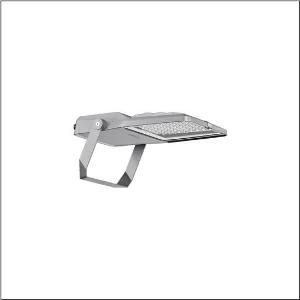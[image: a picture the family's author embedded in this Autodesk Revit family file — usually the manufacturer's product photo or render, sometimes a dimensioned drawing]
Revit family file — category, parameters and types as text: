
# Revit family: floodlight_fl_21_iq_mini___pl64_5xa7772b3e1a_f8e6
name_source: partatom
category: Lighting Fixtures
units: mm (PartAtom-declared; Revit-internal decimal feet)

## family parameters
Cut with Voids When Loaded = No
Host = Face
Light Source = No
Part Type = Normal
Room Calculation Point = No
Round Connector Dimension = Use Diameter
Shared = No

## types (1)
- --- (1 x LED, 5190 lm, 45.5 W, 3000K)
    Apparent Load = 46 VA
    CIE Flux Codes = 28 80 98 100 100
    Color Rendering = 80
    Color Temperature = 3000K
    Default Elevation = 1800 mm
    Description = Floodlight FL 21 iQ mini, floodlight, primary light control with lens, of PMMA, primary optical cover: protective disc, of toughened safety glass, transparent, light distribution: PL64, light emission: direct distribution, installation type: surface-mounted, LED, High Power LED, rated luminous flux: 5.190lm, luminous efficacy: 114lm/W, light colour: 830, colour temperature: 3000K, control: Street-Remote, Auto-Match, Temp-Guard, Night-Set, Smart-Wire, Desk-Remote (wireless, voltage-free reading and setting of iQ features in the workshop via application-optimized NFC function/RFID function), optimised constant luminous flux control (CLO 2.0), with terminal, 6-pole, mains connection: 220..240V, AC, 50/60Hz, start of lifetime: 46W, end of service life: 48W, reduction: 21W, luminaire housing, of diecast aluminium, powder-coated, Siteco® metallic grey (DB 702S), corrosivity category C5 mid according to DIN EN ISO 12944, sealing non-destructively replaceable, mounting bracket, of steel, galvanised, powder-coated, Siteco® metallic grey (DB 702S), protection rating (complete): IP66, insulation class (complete): insulation class II (safety insulation), certification: CE, ENEC, VDE, protection symbol: D, impact resistance: IK08, permissible operating ambient temperature: -40..+40°C, permissible operating ambient temperature for outdoor applications: -40..+50°C, standard: DIN EN 12944, LABS conformity tested according to VDMA 24364:2018-05, packaging unit: 1 piece

Light Distribution: PL64
    Height = 70 mm
    Lamp = 1 x LED
    Lamp Light Flux = 5190 lm
    Lamp Power = 45.5 W
    Lamp count = 1
    Length = 485 mm
    Luminous efficacy = 114 lm/W
    Manufacturer = Siteco
    ModVariant = No
    Model = 5XA7772B3E1A
    Number of Poles = 1
    OnlyDefault = Yes
    Power Factor = 1
    Product Name = Floodlight FL 21 iQ mini | PL64
    Product group = floodlight | pylon annexe
    ProductGroupID = 6200
    Protection Class = Protection class II
    Protection Degree = IP 66
    RLX_Detail_Level = 1
    RLX_Emergency_Light_Flux = 0 lm
    RLX_Emergency_Type = 0
    RLX_Emergency_Type_DB = No
    RlxData = <blob elided: 96129 chars, md5=d5474798>
    Socket = socket
    Standby Power = 0 W
    System Light Flux = 5190 lm
    System Power = 46 W
    Type Comments = factory setting: luminous flux: 100 % | dim-lin: 254 | 463 mA
    Type Image = l_1006845.jpg
    URL = http://relux.com
    VarID = @adj_099165
    Voltage = 0 V
    Weight = 0.00 kg
    Width = 337 mm

## geometry (parser evidence)
native form markers: Blend x4, Sweep x13
no freeform markers — native parametric forms only
